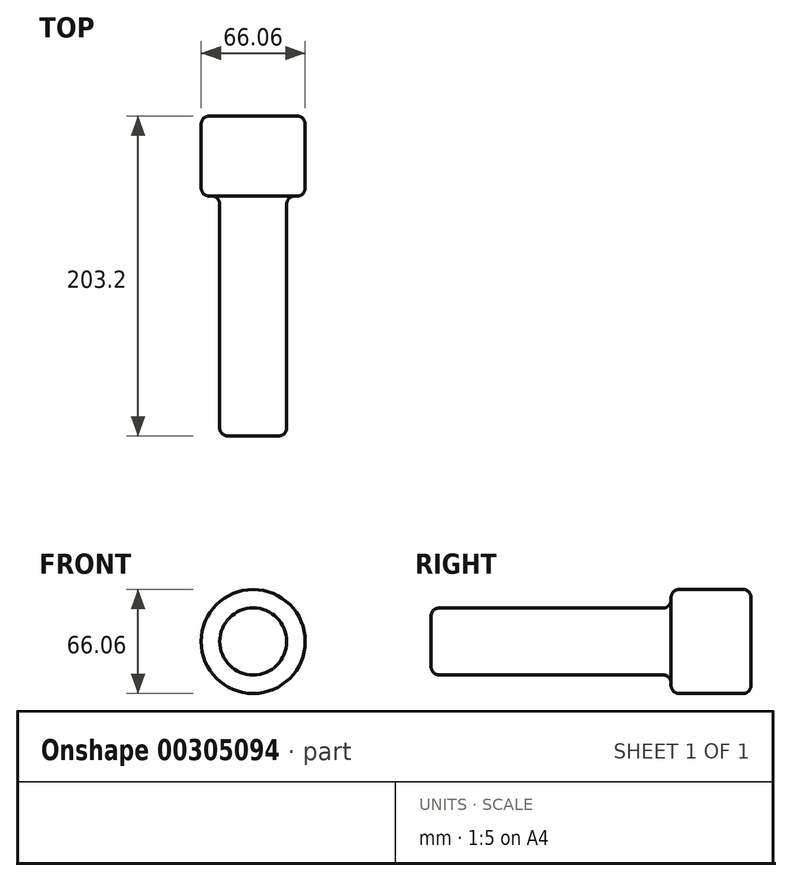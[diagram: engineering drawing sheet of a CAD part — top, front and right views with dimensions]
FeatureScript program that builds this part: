
annotation { "Feature Type Name" : "Feature", "Feature Type Description" : "" }
export const myFeature = defineFeature(function(context is Context, id is Id, definition is map)
    precondition{}
    {
        {
            var Q0;
            Q0=qCreatedBy(makeId("Front.planeOp"),FACE);
            var sketch = newSketch(context, id + "F0", { "sketchPlane" : qUnion([Q0])});
            skCircle(sketch, "E0", {"center": v(0, 0) * mm, "radius": 33.03 * mm});
            skSolve(sketch);
        }
        {
            var Q0;
            Q0 = qSketchRegion(id + "F0", true);
            extrude(context, id + "F1", {"entities" : qUnion([Q0]), "depth" : 50.8 * mm});
        }
        {
            var Q0;
            Q0=qCreatedBy(makeId("Front.planeOp"),FACE);
            var sketch = newSketch(context, id + "F2", { "sketchPlane" : qUnion([Q0])});
            skCircle(sketch, "E1", {"center": v(0, 0) * mm, "radius": 21.25 * mm});
            skSolve(sketch);
        }
        {
            var Q0;
            Q0=makeQuery(id+"F2.imprint","IMPRINT",FACE,{"disambiguationData":[TD([[makeQuery(id+"F2.imprint","IMPRINT",EDGE,{"derivedFrom":sQuery(id+"F2.wireOp",EDGE,"E1")}),1.0]])]});
            extrude(context, id + "F3", {"entities" : qUnion([Q0]), "operationType" : NewBodyOperationType.ADD, "depth" : 203.2 * mm});
        }
        {
            var Q0;
            Q0=makeQuery(id+"F1.opExtrude","CAP_EDGE",EDGE,{"disambiguationData":[OSD([sQuery(id+"F0.wireOp",EDGE,"E0")])],"isStart":true});
            fillet(context, id + "F4", {"entities" : qUnion([Q0]), "radius" : 5.08 * mm, "tangentPropagation" : true, "allowEdgeOverflow" : false});
        }
        {
            var Q0;
            Q0=makeQuery(id+"F1.opExtrude","CAP_EDGE",EDGE,{"disambiguationData":[OSD([sQuery(id+"F0.wireOp",EDGE,"E0")])],"isStart":false});
            fillet(context, id + "F5", {"entities" : qUnion([Q0]), "radius" : 5.08 * mm, "tangentPropagation" : true, "allowEdgeOverflow" : false});
        }
        {
            var Q0;
            Q0=makeQuery(id+"F3.boolean.opBoolean","INTERSECT",EDGE,{"derivedFrom":[makeQuery(id+"F1.opExtrude","CAP_FACE",FACE,{"disambiguationData":[OSD([sQuery(id+"F0.wireOp",EDGE,"E0")])],"isStart":false}),makeQuery(id+"F3.opExtrude","SWEPT_FACE",FACE,{"disambiguationData":[OSD([sQuery(id+"F2.wireOp",EDGE,"E1")])]})]});
            var Q1;
            Q1=makeQuery(id+"F3.opExtrude","CAP_EDGE",EDGE,{"disambiguationData":[OSD([sQuery(id+"F2.wireOp",EDGE,"E1")])],"isStart":false});
            fillet(context, id + "F6", {"entities" : qUnion([Q0, Q1]), "radius" : 5.08 * mm, "tangentPropagation" : true, "allowEdgeOverflow" : false});
        }
    });
